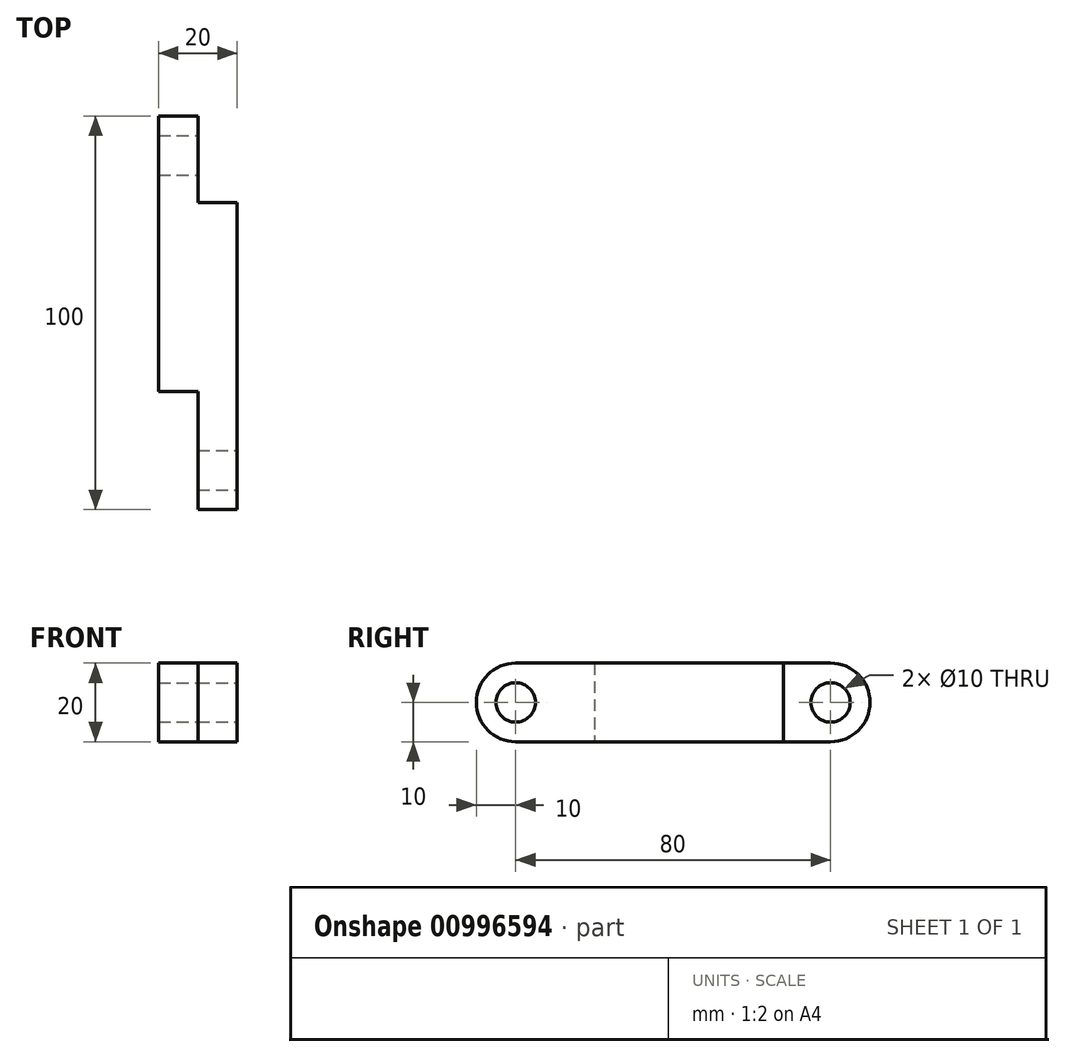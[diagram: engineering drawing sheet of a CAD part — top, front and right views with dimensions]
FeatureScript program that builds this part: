
annotation { "Feature Type Name" : "Feature", "Feature Type Description" : "" }
export const myFeature = defineFeature(function(context is Context, id is Id, definition is map)
    precondition{}
    {
        {
            var Q0;
            Q0=qCreatedBy(makeId("Front.planeOp"),FACE);
            var sketch = newSketch(context, id + "F0", { "sketchPlane" : qUnion([Q0])});
            skLineSegment(sketch, "E0.bottom", {"start": v(-10, 10) * mm, "end": v(10, 10) * mm});
            skLineSegment(sketch, "E0.top", {"start": v(-10, -10) * mm, "end": v(10, -10) * mm});
            skLineSegment(sketch, "E0.left", {"start": v(-10, 10) * mm, "end": v(-10, -10) * mm});
            skLineSegment(sketch, "E0.right", {"start": v(10, 10) * mm, "end": v(10, -10) * mm});
            skSolve(sketch);
        }
        {
            var Q0;
            Q0=makeQuery(id+"F0.imprint","IMPRINT",FACE,{"disambiguationData":[TD([[makeQuery(id+"F0.imprint","IMPRINT",EDGE,{"derivedFrom":sQuery(id+"F0.wireOp",EDGE,"E0.bottom")}),-1.0]])]});
            extrude(context, id + "F1", {"entities" : qUnion([Q0]), "depth" : 100 * mm, "offsetDistance" : 25 * mm});
        }
        {
            var Q0;
            Q0=makeQuery(id+"F1.opExtrude","SWEPT_FACE",FACE,{"disambiguationData":[OSD([sQuery(id+"F0.wireOp",EDGE,"E0.right")])]});
            var sketch = newSketch(context, id + "F2", { "sketchPlane" : qUnion([Q0])});
            skCircle(sketch, "E1", {"center": v(-90, 0) * mm, "radius": 5 * mm});
            skSolve(sketch);
        }
        {
            var Q0;
            Q0=makeQuery(id+"F2.imprint","IMPRINT",FACE,{"disambiguationData":[TD([[makeQuery(id+"F2.imprint","IMPRINT",EDGE,{"derivedFrom":sQuery(id+"F2.wireOp",EDGE,"E1")}),1.0]])]});
            extrude(context, id + "F3", {"entities" : qUnion([Q0]), "operationType" : NewBodyOperationType.REMOVE, "endBound" : BoundingType.THROUGH_ALL, "oppositeDirection" : true, "depth" : 25 * mm, "offsetDistance" : 25 * mm});
        }
        {
            var Q0;
            Q0=makeQuery(id+"F1.opExtrude","SWEPT_FACE",FACE,{"disambiguationData":[OSD([sQuery(id+"F0.wireOp",EDGE,"E0.right")])]});
            var sketch = newSketch(context, id + "F4", { "sketchPlane" : qUnion([Q0])});
            skCircle(sketch, "E2", {"center": v(-10, 0) * mm, "radius": 5 * mm});
            skSolve(sketch);
        }
        {
            var Q0;
            Q0=makeQuery(id+"F4.imprint","IMPRINT",FACE,{"disambiguationData":[TD([[makeQuery(id+"F4.imprint","IMPRINT",EDGE,{"derivedFrom":sQuery(id+"F4.wireOp",EDGE,"E2")}),1.0]])]});
            extrude(context, id + "F5", {"entities" : qUnion([Q0]), "operationType" : NewBodyOperationType.REMOVE, "endBound" : BoundingType.THROUGH_ALL, "oppositeDirection" : true, "depth" : 25 * mm, "offsetDistance" : 25 * mm});
        }
        {
            var Q0;
            Q0=makeQuery(id+"F1.opExtrude","SWEPT_FACE",FACE,{"disambiguationData":[OSD([sQuery(id+"F0.wireOp",EDGE,"E0.right")])]});
            var sketch = newSketch(context, id + "F6", { "sketchPlane" : qUnion([Q0])});
            skLineSegment(sketch, "E3.bottom", {"start": v(0, -10) * mm, "end": v(-22, -10) * mm});
            skLineSegment(sketch, "E3.top", {"start": v(0, 10) * mm, "end": v(-22, 10) * mm});
            skLineSegment(sketch, "E3.left", {"start": v(0, -10) * mm, "end": v(0, 10) * mm});
            skLineSegment(sketch, "E3.right", {"start": v(-22, -10) * mm, "end": v(-22, 10) * mm});
            skSolve(sketch);
        }
        {
            var Q0;
            Q0=makeQuery(id+"F6.imprint","IMPRINT",FACE,{"disambiguationData":[TD([[makeQuery(id+"F6.imprint","IMPRINT",EDGE,{"derivedFrom":sQuery(id+"F6.wireOp",EDGE,"E3.bottom")}),1.0]])]});
            extrude(context, id + "F7", {"entities" : qUnion([Q0]), "operationType" : NewBodyOperationType.REMOVE, "oppositeDirection" : true, "depth" : 10 * mm, "offsetDistance" : 25 * mm});
        }
        {
            var Q0;
            Q0=makeQuery(id+"F1.opExtrude","SWEPT_FACE",FACE,{"disambiguationData":[OSD([sQuery(id+"F0.wireOp",EDGE,"E0.left")])]});
            var sketch = newSketch(context, id + "F8", { "sketchPlane" : qUnion([Q0])});
            skLineSegment(sketch, "E4.bottom", {"start": v(100, 10) * mm, "end": v(70, 10) * mm});
            skLineSegment(sketch, "E4.top", {"start": v(100, -10) * mm, "end": v(70, -10) * mm});
            skLineSegment(sketch, "E4.left", {"start": v(100, 10) * mm, "end": v(100, -10) * mm});
            skLineSegment(sketch, "E4.right", {"start": v(70, 10) * mm, "end": v(70, -10) * mm});
            skSolve(sketch);
        }
        {
            var Q0;
            Q0=makeQuery(id+"F8.imprint","IMPRINT",FACE,{"disambiguationData":[TD([[makeQuery(id+"F8.imprint","IMPRINT",EDGE,{"derivedFrom":sQuery(id+"F8.wireOp",EDGE,"E4.bottom")}),1.0]])]});
            extrude(context, id + "F9", {"entities" : qUnion([Q0]), "operationType" : NewBodyOperationType.REMOVE, "oppositeDirection" : true, "depth" : 10 * mm, "offsetDistance" : 25 * mm});
        }
        {
            var Q0;
            Q0=makeQuery(id+"F1.opExtrude","CAP_EDGE",EDGE,{"disambiguationData":[OSD([sQuery(id+"F0.wireOp",EDGE,"E0.bottom")])],"isStart":false});
            var Q1;
            Q1=makeQuery(id+"F1.opExtrude","CAP_EDGE",EDGE,{"disambiguationData":[OSD([sQuery(id+"F0.wireOp",EDGE,"E0.top")])],"isStart":false});
            var Q2;
            Q2=makeQuery(id+"F1.opExtrude","CAP_EDGE",EDGE,{"disambiguationData":[OSD([sQuery(id+"F0.wireOp",EDGE,"E0.top")])],"isStart":true});
            var Q3;
            Q3=makeQuery(id+"F1.opExtrude","CAP_EDGE",EDGE,{"disambiguationData":[OSD([sQuery(id+"F0.wireOp",EDGE,"E0.bottom")])],"isStart":true});
            fillet(context, id + "F10", {"entities" : qUnion([Q0, Q1, Q2, Q3]), "radius" : 10 * mm, "tangentPropagation" : true, "allowEdgeOverflow" : false});
        }
    });
